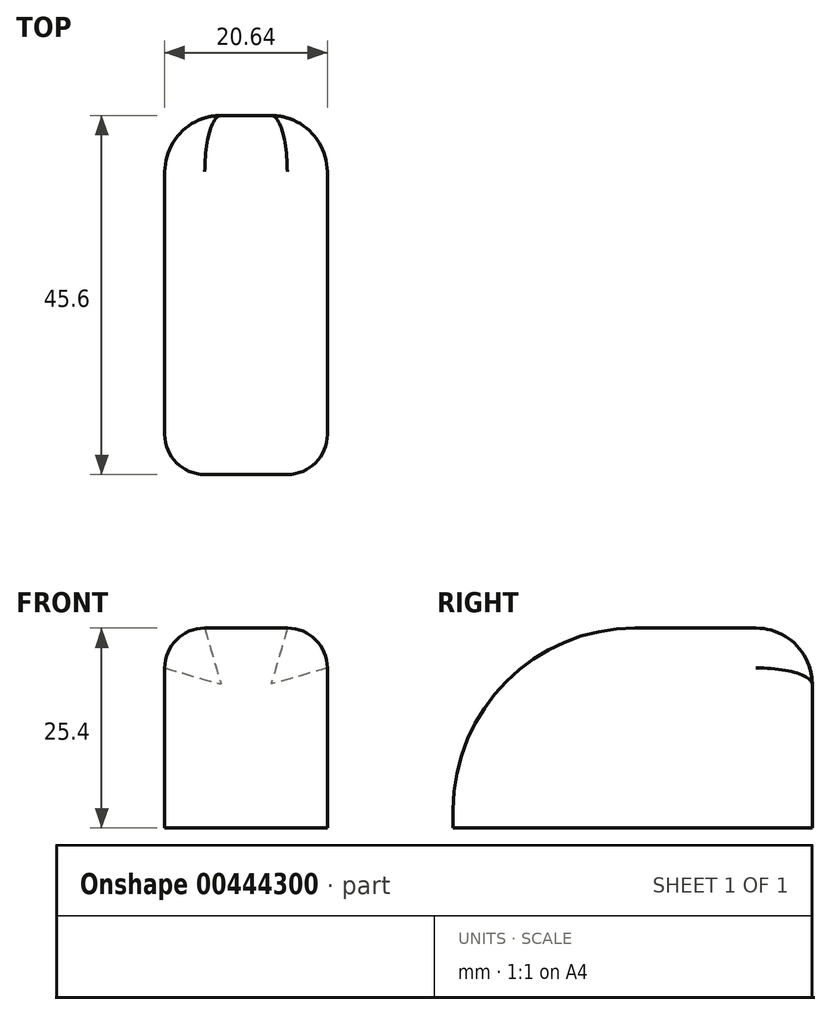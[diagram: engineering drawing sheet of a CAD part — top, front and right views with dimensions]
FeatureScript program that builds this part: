
annotation { "Feature Type Name" : "Feature", "Feature Type Description" : "" }
export const myFeature = defineFeature(function(context is Context, id is Id, definition is map)
    precondition{}
    {
        {
            var Q0;
            Q0=qCreatedBy(makeId("Top.planeOp"),FACE);
            var sketch = newSketch(context, id + "F0", { "sketchPlane" : qUnion([Q0])});
            skLineSegment(sketch, "E0.bottom", {"start": v(10.32, -22.8) * mm, "end": v(-10.32, -22.8) * mm});
            skLineSegment(sketch, "E0.top", {"start": v(10.32, 22.8) * mm, "end": v(-10.32, 22.8) * mm});
            skLineSegment(sketch, "E0.left", {"start": v(10.32, -22.8) * mm, "end": v(10.32, 22.8) * mm});
            skLineSegment(sketch, "E0.right", {"start": v(-10.32, -22.8) * mm, "end": v(-10.32, 22.8) * mm});
            skPoint(sketch, "E0.middle", {"position": v(0, 0) * mm});
            skSolve(sketch);
        }
        {
            var Q0;
            Q0 = qSketchRegion(id + "F0", true);
            extrude(context, id + "F1", {"entities" : qUnion([Q0]), "depth" : 25.4 * mm});
        }
        {
            var Q0;
            Q0=makeQuery(id+"F1.opExtrude","CAP_EDGE",EDGE,{"disambiguationData":[OSD([sQuery(id+"F0.wireOp",EDGE,"E0.bottom")])],"isStart":false});
            fillet(context, id + "F2", {"entities" : qUnion([Q0]), "radius" : 23.1 * mm, "tangentPropagation" : true, "allowEdgeOverflow" : false});
        }
        {
            var Q0;
            Q0=makeQuery(id+"F1.opExtrude","CAP_EDGE",EDGE,{"disambiguationData":[OSD([sQuery(id+"F0.wireOp",EDGE,"E0.left")])],"isStart":false});
            fillet(context, id + "F3", {"entities" : qUnion([Q0]), "radius" : 5.08 * mm, "tangentPropagation" : true, "allowEdgeOverflow" : false});
        }
        {
            var Q0;
            Q0=makeQuery(id+"F1.opExtrude","CAP_EDGE",EDGE,{"disambiguationData":[OSD([sQuery(id+"F0.wireOp",EDGE,"E0.right")])],"isStart":false});
            fillet(context, id + "F4", {"entities" : qUnion([Q0]), "radius" : 5.08 * mm, "tangentPropagation" : true, "allowEdgeOverflow" : false});
        }
        {
            var Q0;
            Q0=makeQuery(id+"F1.opExtrude","CAP_EDGE",EDGE,{"disambiguationData":[OSD([sQuery(id+"F0.wireOp",EDGE,"E0.top")])],"isStart":false});
            fillet(context, id + "F5", {"entities" : qUnion([Q0]), "radius" : 7.13 * mm, "tangentPropagation" : true, "allowEdgeOverflow" : false});
        }
    });
